# Revit family: ACRUD
name_source: partatom
category: Mechanical Equipment
units: mm (PartAtom-declared; Revit-internal decimal feet)

## family parameters
Always vertical = Yes
Cut with Voids When Loaded = No
Part Type = Normal
Room Calculation Point = No
Round Connector Dimension = Use Diameter
Shared = No
Work Plane-Based = No

## types (54) — shared parameters
1.5" = 1 1/2"
2" = 2"
Manufacturer = Loren Cook Company
ONE EIGTH = 1/8"
URL = www.lorencook.com
ZERO = 0"

## per-type parameters (varying)
| type | APLUSG | A_SUB | B_SUB | C_SUB | DEPTH | EDGE_TO_CURB | EIGHTH_T_SQ | HALF_B_SUB | INLET_HEIGHT | Model | RO/2 | ROOF_OPENING | T_SQ | T_SQ_HALF | Type Comments | WB_RADIUS | a_sub_minus_3 |
| 100_ACRUD | 2 1/8" | 13 1/2" | 21 1/8" | 16 3/8" | 2" | 2 5/16" | 1 13/16" | 10 9/16" | 1/8" | ACRUD | 6 3/4" | 13 1/2" | 18" | 9" | Upblast Centrifugal Exhaust Ventilator Roof Mounted/Direct Drive | 4" | 10 1/2" |
| 120_ACRUD | 3 13/16" | 19 1/16" | 30 3/16" | 28 1/8" | 2" | 2 5/16" | 2" | 15 3/32" | 1 13/16" | ACRUD | 7 3/4" | 15 1/2" | 20" | 10" | Upblast Centrifugal Exhaust Ventilator Roof Mounted/Direct Drive | 6" | 16 1/16" |
| 135_ACRUD | 4 3/16" | 19 1/16" | 30 3/16" | 28 5/8" | 2" | 2 5/16" | 2" | 15 3/32" | 2 3/16" | ACRUD | 7 3/4" | 15 1/2" | 20" | 10" | Upblast Centrifugal Exhaust Ventilator Roof Mounted/Direct Drive | 6" | 16 1/16" |
| 150_ACRUD | 5 1/16" | 20 15/16" | 34 11/16" | 30 1/4" | 2" | 2 5/16" | 2 13/32" | 17 11/32" | 3 1/16" | ACRUD | 9 3/4" | 19 1/2" | 24" | 12" | Upblast Centrifugal Exhaust Ventilator Roof Mounted/Direct Drive | 6" | 17 15/16" |
| 165_ACRUD | 5 9/16" | 20 15/16" | 34 11/16" | 30 3/4" | 2" | 2 5/16" | 2 13/32" | 17 11/32" | 3 9/16" | ACRUD | 9 3/4" | 19 1/2" | 24" | 12" | Upblast Centrifugal Exhaust Ventilator Roof Mounted/Direct Drive | 6" | 17 15/16" |
| 180_ACRUD | 6 15/16" | 24 13/16" | 39 7/16" | 35 7/8" | 3" | 2 5/16" | 3" | 19 23/32" | 3 15/16" | ACRUD | 12 3/4" | 25 1/2" | 30" | 15" | Upblast Centrifugal Exhaust Ventilator Roof Mounted/Direct Drive | 6" | 21 13/16" |
| 150_ACRUD-HP | 5 1/16" | 20 15/16" | 34 11/16" | 27 1/2" | 2" | 2 5/16" | 2 13/32" | 17 11/32" | 3 1/16" | ACRUD-HP | 9 3/4" | 19 1/2" | 24" | 12" | Upblast Centrifugal Exhaust Ventilator Roof Mounted/Direct Drive | 6" | 17 15/16" |
| 165_ACRUD-HP | 5 9/16" | 20 15/16" | 34 11/16" | 27 3/4" | 2" | 2 5/16" | 2 13/32" | 17 11/32" | 3 9/16" | ACRUD-HP | 9 3/4" | 19 1/2" | 24" | 12" | Upblast Centrifugal Exhaust Ventilator Roof Mounted/Direct Drive | 6" | 17 15/16" |
| 180_ACRUD-HP | 6 15/16" | 24 13/16" | 39 7/16" | 33 3/8" | 3" | 2 5/16" | 3" | 19 23/32" | 3 15/16" | ACRUD-HP | 12 3/4" | 25 1/2" | 30" | 15" | Upblast Centrifugal Exhaust Ventilator Roof Mounted/Direct Drive | 6" | 21 13/16" |
| 195_ACRUD-HP | 7 7/16" | 24 13/16" | 39 7/16" | 33 1/2" | 3" | 2 5/16" | 3" | 19 23/32" | 4 7/16" | ACRUD-HP | 12 3/4" | 25 1/2" | 30" | 15" | Upblast Centrifugal Exhaust Ventilator Roof Mounted/Direct Drive | 7" | 21 13/16" |
| 165_ACRUD-XP | 5 9/16" | 20 15/16" | 34 11/16" | 26 11/16" | 2" | 2 5/16" | 2 13/32" | 17 11/32" | 3 9/16" | ACRUD-XP | 9 3/4" | 19 1/2" | 24" | 12" | Upblast Centrifugal Exhaust Ventilator Roof Mounted/Direct Drive | 6" | 17 15/16" |
| 180_ACRUD-XP | 6 15/16" | 24 13/16" | 39 7/16" | 31 9/16" | 3" | 2 5/16" | 3" | 19 23/32" | 3 15/16" | ACRUD-XP | 12 3/4" | 25 1/2" | 30" | 15" | Upblast Centrifugal Exhaust Ventilator Roof Mounted/Direct Drive | 6" | 21 13/16" |
| 195_ACRUD-XP | 7 7/16" | 24 13/16" | 39 7/16" | 32 1/8" | 3" | 2 1/4" | 3" | 19 23/32" | 4 7/16" | ACRUD-XP | 12 3/4" | 25 1/2" | 30" | 15" | Upblast Centrifugal Exhaust Ventilator Roof Mounted/Direct Drive | 7" | 21 13/16" |
| 70_ACRUD | 2 1/8" | 11" | 17 1/8" | 13 3/8" | 2" | 2 5/16" | 1 13/16" | 8 9/16" | 1/8" | ACRUD | 6 3/4" | 13 1/2" | 18" | 9" | Upblast Centrifugal Exhaust Ventilator Roof Mounted/Direct Drive | 2" | 8" |
| 90_ACRUD | 2 1/8" | 13 1/2" | 21 1/8" | 16 3/8" | 2" | 2 5/16" | 1 13/16" | 10 9/16" | 1/8" | ACRUD | 6 3/4" | 13 1/2" | 18" | 9" | Upblast Centrifugal Exhaust Ventilator Roof Mounted/Direct Drive | 4" | 10 1/2" |
| 195_ACRUD | 7 7/16" | 24 13/16" | 39 7/16" | 36 3/8" | 3" | 2 1/4" | 3" | 19 23/32" | 4 7/16" | ACRUD | 12 3/4" | 25 1/2" | 30" | 15" | Upblast Centrifugal Exhaust Ventilator Roof Mounted/Direct Drive | 7" | 21 13/16" |
| 210_ACRUD | 7 7/16" | 25 15/16" | 45 1/4" | 38 3/8" | 3" | 2 1/4" | 3" | 22 5/8" | 4 7/16" | ACRUD | 12 3/4" | 25 1/2" | 30" | 15" | Upblast Centrifugal Exhaust Ventilator Roof Mounted/Direct Drive | 7" | 22 15/16" |
| 225_ACRUD | 7 7/16" | 25 15/16" | 45 1/4" | 38 1/8" | 3" | 2 1/4" | 3" | 22 5/8" | 4 7/16" | ACRUD | 12 3/4" | 25 1/2" | 30" | 15" | Upblast Centrifugal Exhaust Ventilator Roof Mounted/Direct Drive | 7" | 22 15/16" |
| 245_ACRUD | 7 7/16" | 28 1/2" | 49 1/4" | 41 11/16" | 3" | 2 1/4" | 3" | 24 5/8" | 4 7/16" | ACRUD | 12 3/4" | 25 1/2" | 30" | 15" | Upblast Centrifugal Exhaust Ventilator Roof Mounted/Direct Drive | 7" | 25 1/2" |
| 270_ACRUD | 7 7/16" | 28 1/2" | 49 1/4" | 41 11/16" | 3" | 2 1/4" | 3 19/32" | 24 5/8" | 4 7/16" | ACRUD | 15 3/4" | 31 1/2" | 36" | 18" | Upblast Centrifugal Exhaust Ventilator Roof Mounted/Direct Drive | 7" | 25 1/2" |
| 300_ACRUD | 7 7/16" | 33 7/8" | 54 1/4" | 49 15/16" | 3" | 2 1/4" | 3 19/32" | 27 1/8" | 4 7/16" | ACRUD | 15 3/4" | 31 1/2" | 36" | 18" | Upblast Centrifugal Exhaust Ventilator Roof Mounted/Direct Drive | 7" | 30 7/8" |
| 210_ACRUD-HP | 7 7/16" | 25 15/16" | 45 1/4" | 35 3/8" | 3" | 2 1/4" | 3" | 22 5/8" | 4 7/16" | ACRUD-HP | 12 3/4" | 25 1/2" | 30" | 15" | Upblast Centrifugal Exhaust Ventilator Roof Mounted/Direct Drive | 7" | 22 15/16" |
| 225_ACRUD-HP | 7 7/16" | 25 15/16" | 45 1/4" | 35 1/2" | 3" | 2 1/4" | 3" | 22 5/8" | 4 7/16" | ACRUD-HP | 12 3/4" | 25 1/2" | 30" | 15" | Upblast Centrifugal Exhaust Ventilator Roof Mounted/Direct Drive | 7" | 22 15/16" |
| 245_ACRUD-HP | 7 7/16" | 28 1/2" | 49 1/4" | 34 1/16" | 3" | 2 1/4" | 3" | 24 5/8" | 4 7/16" | ACRUD-HP | 12 3/4" | 25 1/2" | 30" | 15" | Upblast Centrifugal Exhaust Ventilator Roof Mounted/Direct Drive | 7" | 25 1/2" |
| 270_ACRUD-HP | 7 7/16" | 28 1/2" | 49 1/4" | 37 5/16" | 3" | 2 1/4" | 3 19/32" | 24 5/8" | 4 7/16" | ACRUD-HP | 15 3/4" | 31 1/2" | 36" | 18" | Upblast Centrifugal Exhaust Ventilator Roof Mounted/Direct Drive | 7" | 25 1/2" |
| 300_ACRUD-HP | 7 7/16" | 33 7/8" | 54 1/4" | 45 15/16" | 3" | 2 1/4" | 3 19/32" | 27 1/8" | 4 7/16" | ACRUD-HP | 15 3/4" | 31 1/2" | 36" | 18" | Upblast Centrifugal Exhaust Ventilator Roof Mounted/Direct Drive | 7" | 30 7/8" |
| 210_ACRUD-XP | 7 7/16" | 25 15/16" | 45 1/4" | 32 3/4" | 3" | 2 1/4" | 3" | 22 5/8" | 4 7/16" | ACRUD-XP | 12 3/4" | 25 1/2" | 30" | 15" | Upblast Centrifugal Exhaust Ventilator Roof Mounted/Direct Drive | 7" | 22 15/16" |
| 225_ACRUD-XP | 7 7/16" | 25 15/16" | 45 1/4" | 33 5/16" | 3" | 2 1/4" | 3" | 22 5/8" | 4 7/16" | ACRUD-XP | 12 3/4" | 25 1/2" | 30" | 15" | Upblast Centrifugal Exhaust Ventilator Roof Mounted/Direct Drive | 7" | 22 15/16" |
| 245_ACRUD-XP | 7 7/16" | 28 1/2" | 49 1/4" | 34 1/16" | 3" | 2 1/4" | 3" | 24 5/8" | 4 7/16" | ACRUD-XP | 12 3/4" | 25 1/2" | 30" | 15" | Upblast Centrifugal Exhaust Ventilator Roof Mounted/Direct Drive | 7" | 25 1/2" |
| 270_ACRUD-XP | 7 7/16" | 28 1/2" | 49 1/4" | 35" | 3" | 2 1/4" | 3 19/32" | 24 5/8" | 4 7/16" | ACRUD-XP | 15 3/4" | 31 1/2" | 36" | 18" | Upblast Centrifugal Exhaust Ventilator Roof Mounted/Direct Drive | 7" | 25 1/2" |
| 300_ACRUD-XP | 7 7/16" | 33 7/8" | 54 1/4" | 41 7/16" | 3" | 2 1/4" | 3 19/32" | 27 1/8" | 4 7/16" | ACRUD-XP | 15 3/4" | 31 1/2" | 36" | 18" | Upblast Centrifugal Exhaust Ventilator Roof Mounted/Direct Drive | 7" | 30 7/8" |
| 150_ACRUD-EC | 5 1/16" | 20 15/16" | 34 11/16" | 30 1/4" | 2" | 2 5/16" | 2 13/32" | 17 11/32" | 3 1/16" | ACRUDEC | 9 3/4" | 19 1/2" | 24" | 12" | Upblast Centrifugal Exhaust Ventilator Roof Mounted/Direct Drive with External Speed Control Electronically Commutated (EC) Motor Type N | 6" | 17 15/16" |
| 195_ACRUD-XP-EC | 7 7/16" | 24 13/16" | 39 7/16" | 32 1/8" | 3" | 2 1/4" | 3" | 19 23/32" | 4 7/16" | ACRXDEC | 12 3/4" | 25 1/2" | 30" | 15" | Upblast Centrifugal Exhaust Ventilator Roof Mounted/Direct Drive with External Speed Control Electronically Commutated (EC) Motor Type N | 7" | 21 13/16" |
| 150_ACRUD-HP-VF | 5 1/16" | 20 15/16" | 34 11/16" | 27 1/2" | 2" | 2 5/16" | 2 13/32" | 17 11/32" | 3 1/16" | ACRUD-HP-VF | 9 3/4" | 19 1/2" | 24" | 12" | Upblast Centrifugal Exhaust Ventilator Roof Mounted/Direct Drive Electronically Commutated Vari-Flow Motor | 6" | 17 15/16" |
| 165_ACRUD-HP-VF | 5 9/16" | 20 15/16" | 34 11/16" | 27 3/4" | 2" | 2 5/16" | 2 13/32" | 17 11/32" | 3 9/16" | ACRUD-HP-VF | 9 3/4" | 19 1/2" | 24" | 12" | Upblast Centrifugal Exhaust Ventilator Roof Mounted/Direct Drive Electronically Commutated Vari-Flow Motor | 6" | 17 15/16" |
| 180_ACRUD-HP-VF | 6 15/16" | 24 13/16" | 39 7/16" | 33 3/8" | 3" | 2 5/16" | 3" | 19 23/32" | 3 15/16" | ACRUD-HP-VF | 12 3/4" | 25 1/2" | 30" | 15" | Upblast Centrifugal Exhaust Ventilator Roof Mounted/Direct Drive Electronically Commutated Vari-Flow Motor | 6" | 21 13/16" |
| 195_ACRUD-HP-VF | 7 7/16" | 24 13/16" | 39 7/16" | 33 1/2" | 3" | 2 5/16" | 3" | 19 23/32" | 4 7/16" | ACRUD-HP-VF | 12 3/4" | 25 1/2" | 30" | 15" | Upblast Centrifugal Exhaust Ventilator Roof Mounted/Direct Drive Electronically Commutated Vari-Flow Motor | 7" | 21 13/16" |
| 210_ACRUD-HP-VF | 7 7/16" | 25 15/16" | 45 1/4" | 35 3/8" | 3" | 2 1/4" | 3" | 22 5/8" | 4 7/16" | ACRUD-HP-VF | 12 3/4" | 25 1/2" | 30" | 15" | Upblast Centrifugal Exhaust Ventilator Roof Mounted/Direct Drive Electronically Commutated Vari-Flow Motor | 7" | 22 15/16" |
| 100_ACRUD-VF | 2 1/8" | 13 1/2" | 21 1/8" | 16 3/8" | 2" | 2 5/16" | 1 13/16" | 10 9/16" | 1/8" | ACRUD-VF | 6 3/4" | 13 1/2" | 18" | 9" | Upblast Centrifugal Exhaust Ventilator Roof Mounted/Direct Drive Electronically Commutated Vari-Flow Motor | 4" | 10 1/2" |
| 120_ACRUD-VF | 3 13/16" | 19 1/16" | 30 3/16" | 28 1/8" | 2" | 2 5/16" | 2" | 15 3/32" | 1 13/16" | ACRUD-VF | 7 3/4" | 15 1/2" | 20" | 10" | Upblast Centrifugal Exhaust Ventilator Roof Mounted/Direct Drive Electronically Commutated Vari-Flow Motor | 6" | 16 1/16" |
| 135_ACRUD-VF | 4 3/16" | 19 1/16" | 30 3/16" | 28 5/8" | 2" | 2 5/16" | 2" | 15 3/32" | 2 3/16" | ACRUD-VF | 7 3/4" | 15 1/2" | 20" | 10" | Upblast Centrifugal Exhaust Ventilator Roof Mounted/Direct Drive Electronically Commutated Vari-Flow Motor | 6" | 16 1/16" |
| 150_ACRUD-VF | 5 1/16" | 20 15/16" | 34 11/16" | 30 1/4" | 2" | 2 5/16" | 2 13/32" | 17 11/32" | 3 1/16" | ACRUD-VF | 9 3/4" | 19 1/2" | 24" | 12" | Upblast Centrifugal Exhaust Ventilator Roof Mounted/Direct Drive Electronically Commutated Vari-Flow Motor | 6" | 17 15/16" |
| 165_ACRUD-VF | 5 9/16" | 20 15/16" | 34 11/16" | 30 3/4" | 2" | 2 5/16" | 2 13/32" | 17 11/32" | 3 9/16" | ACRUD-VF | 9 3/4" | 19 1/2" | 24" | 12" | Upblast Centrifugal Exhaust Ventilator Roof Mounted/Direct Drive Electronically Commutated Vari-Flow Motor | 6" | 17 15/16" |
| 180_ACRUD-VF | 6 15/16" | 24 13/16" | 39 7/16" | 35 7/8" | 3" | 2 5/16" | 3" | 19 23/32" | 3 15/16" | ACRUD-VF | 12 3/4" | 25 1/2" | 30" | 15" | Upblast Centrifugal Exhaust Ventilator Roof Mounted/Direct Drive Electronically Commutated Vari-Flow Motor | 6" | 21 13/16" |
| 195_ACRUD-VF | 7 7/16" | 24 13/16" | 39 7/16" | 36 3/8" | 3" | 2 1/4" | 3" | 19 23/32" | 4 7/16" | ACRUD-VF | 12 3/4" | 25 1/2" | 30" | 15" | Upblast Centrifugal Exhaust Ventilator Roof Mounted/Direct Drive Electronically Commutated Vari-Flow Motor | 7" | 21 13/16" |
| 210_ACRUD-VF | 7 7/16" | 25 15/16" | 45 1/4" | 38 3/8" | 3" | 2 1/4" | 3" | 22 5/8" | 4 7/16" | ACRUD-VF | 12 3/4" | 25 1/2" | 30" | 15" | Upblast Centrifugal Exhaust Ventilator Roof Mounted/Direct Drive Electronically Commutated Vari-Flow Motor | 7" | 22 15/16" |
| 165_ACRUD-XP-VF | 5 9/16" | 20 15/16" | 34 11/16" | 26 11/16" | 2" | 2 5/16" | 2 13/32" | 17 11/32" | 3 9/16" | ACRUD-XP-VF | 9 3/4" | 19 1/2" | 24" | 12" | Upblast Centrifugal Exhaust Ventilator Roof Mounted/Direct Drive Electronically Commutated Vari-Flow Motor | 6" | 17 15/16" |
| 180_ACRUD-XP-VF | 6 15/16" | 24 13/16" | 39 7/16" | 31 9/16" | 3" | 2 5/16" | 3" | 19 23/32" | 3 15/16" | ACRUD-XP-VF | 12 3/4" | 25 1/2" | 30" | 15" | Upblast Centrifugal Exhaust Ventilator Roof Mounted/Direct Drive Electronically Commutated Vari-Flow Motor | 6" | 21 13/16" |
| 195_ACRUD-XP-VF | 7 7/16" | 24 13/16" | 39 7/16" | 32 1/8" | 3" | 2 1/4" | 3" | 19 23/32" | 4 7/16" | ACRUD-XP-VF | 12 3/4" | 25 1/2" | 30" | 15" | Upblast Centrifugal Exhaust Ventilator Roof Mounted/Direct Drive Electronically Commutated Vari-Flow Motor | 7" | 21 13/16" |
| 210_ACRUD-XP-VF | 7 7/16" | 25 15/16" | 45 1/4" | 32 3/4" | 3" | 2 1/4" | 3" | 22 5/8" | 4 7/16" | ACRUD-XP-VF | 12 3/4" | 25 1/2" | 30" | 15" | Upblast Centrifugal Exhaust Ventilator Roof Mounted/Direct Drive Electronically Commutated Vari-Flow Motor | 7" | 22 15/16" |
| 225_ACRUD-XP-VF | 7 7/16" | 25 15/16" | 45 1/4" | 33 5/16" | 3" | 2 1/4" | 3" | 22 5/8" | 4 7/16" | ACRUD-XP-VF | 12 3/4" | 25 1/2" | 30" | 15" | Upblast Centrifugal Exhaust Ventilator Roof Mounted/Direct Drive Electronically Commutated Vari-Flow Motor | 7" | 22 15/16" |
| 165_ACRUD-HP-EC | 5 9/16" | 20 15/16" | 34 11/16" | 27 3/4" | 2" | 2 5/16" | 2 13/32" | 17 11/32" | 3 9/16" | ACRUD-HP-EC | 9 3/4" | 19 1/2" | 24" | 12" | Upblast Centrifugal Exhaust Ventilator Roof Mounted/Direct Drive with External Speed Control Electronically Commutated (EC) Motor Type N | 6" | 17 15/16" |
| 101_ACRUD | 2 1/8" | 12 1/2" | 24 1/4" | 20 3/16" | 2" | 2 5/16" | 1 13/16" | 12 1/8" | 1/8" | ACRUD | 6 3/4" | 13 1/2" | 18" | 9" | Upblast Centrifugal Exhaust Ventilator Roof Mounted/Direct Drive | 4" | 9 1/2" |
| 101_ACRUD-VF | 3 13/16" | 12 1/2" | 24 1/4" | 20 3/16" | 2" | 2 5/16" | 1 13/16" | 12 1/8" | 1 13/16" | ACRUD-VF | 6 3/4" | 13 1/2" | 18" | 9" | Upblast Centrifugal Exhaust Ventilator Roof Mounted/Direct Drive Electronically Commutated Vari-Flow Motor | 4" | 9 1/2" |

## geometry (parser evidence)
native form markers: Sweep x2
no freeform markers — native parametric forms only
